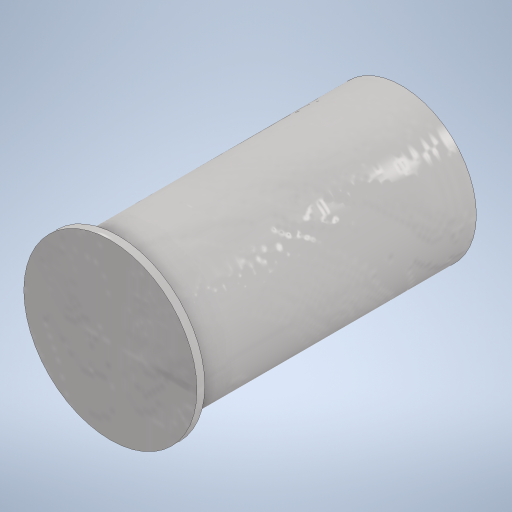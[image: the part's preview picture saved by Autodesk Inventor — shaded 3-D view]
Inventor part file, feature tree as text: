
AUTODESK INVENTOR PART (.ipt)
format: ipt  version: 2024.2 (Build 282272000, 272)  size: 255,488 bytes
history: native  units: mm
features: extrude x2, sketch x2
ambient origin geometry x8: Origin, YZ Plane, XZ Plane, XY Plane, X Axis, Y Axis, Z Axis, Center Point
bodies: Solid1 (feature_tree)
feature tree (4):
  extrude  "Extrusion1"  Depth=18.0mm TaperAngle=0.0deg
  extrude  "Extrusion2"  Depth=0.5mm TaperAngle=0.0deg
  sketch  "Sketch1"  dims[d0=9.5mm d2=18.0mm d3=0.0mm]
  sketch  "Sketch2"  dims[d4=11.0mm d5=0.5mm d6=0.0mm]
